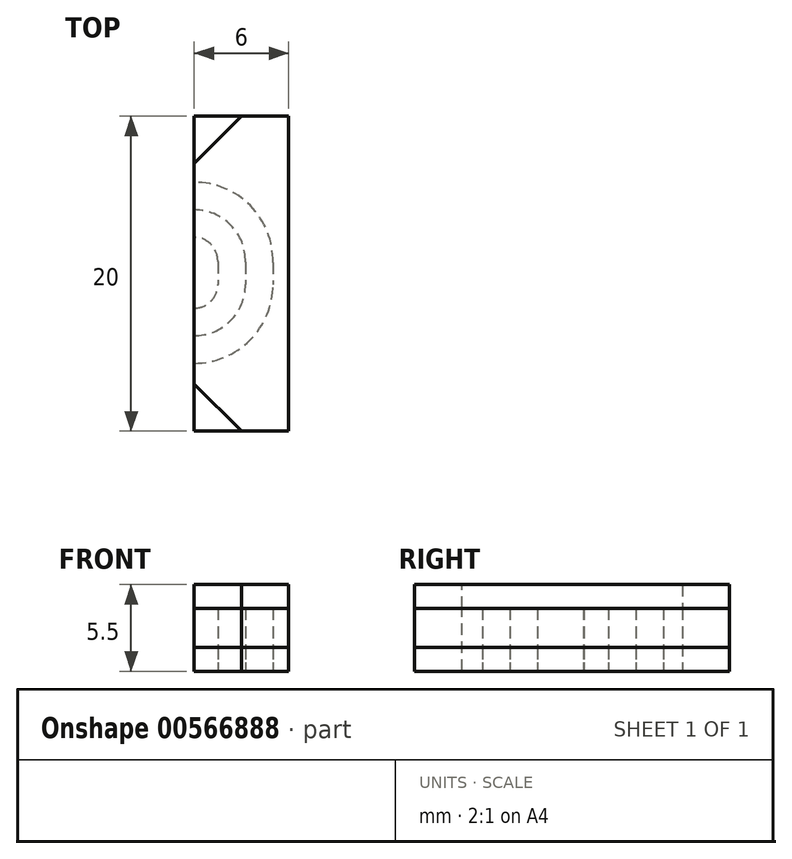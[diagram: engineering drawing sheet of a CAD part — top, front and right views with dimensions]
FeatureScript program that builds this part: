
annotation { "Feature Type Name" : "Feature", "Feature Type Description" : "" }
export const myFeature = defineFeature(function(context is Context, id is Id, definition is map)
    precondition{}
    {
        {
            var Q0;
            Q0=qCreatedBy(makeId("Top.planeOp"),FACE);
            var sketch = newSketch(context, id + "F0", { "sketchPlane" : qUnion([Q0])});
            skLineSegment(sketch, "E0.bottom", {"start": v(3, 10) * mm, "end": v(-3, 10) * mm});
            skLineSegment(sketch, "E0.top", {"start": v(3, -10) * mm, "end": v(-3, -10) * mm});
            skLineSegment(sketch, "E0.left", {"start": v(3, 10) * mm, "end": v(3, -10) * mm});
            skLineSegment(sketch, "E0.right", {"start": v(-3, 10) * mm, "end": v(-3, 5.81) * mm});
            skPoint(sketch, "E0.middle", {"position": v(0, 0) * mm});
            skArc(sketch, "E1", {"start": v(-1.5, 0.76) * mm, "mid": v(-1.92, 1.86) * mm, "end": v(-3, 2.31) * mm});
            skArc(sketch, "E2", {"start": v(-3, -2.19) * mm, "mid": v(-1.94, -1.75) * mm, "end": v(-1.5, -0.69) * mm});
            skLineSegment(sketch, "E3", {"start": v(-1.5, 0.76) * mm, "end": v(-1.5, -0.69) * mm});
            skLineSegment(sketch, "E4.trimOffspring", {"start": v(-3, -2.19) * mm, "end": v(-3, -3.94) * mm});
            skArc(sketch, "E5.0", {"start": v(-3, -3.94) * mm, "mid": v(-0.7, -2.99) * mm, "end": v(0.25, -0.69) * mm});
            skLineSegment(sketch, "E5.1", {"start": v(0.25, 0.74) * mm, "end": v(0.25, -0.69) * mm});
            skArc(sketch, "E5.2", {"start": v(0.25, 0.74) * mm, "mid": v(-0.68, 3.08) * mm, "end": v(-3, 4.06) * mm});
            skArc(sketch, "E6.0", {"start": v(2, 0.73) * mm, "mid": v(0.57, 4.32) * mm, "end": v(-3, 5.81) * mm});
            skLineSegment(sketch, "E6.1", {"start": v(2, 0.73) * mm, "end": v(2, -0.69) * mm});
            skArc(sketch, "E6.2", {"start": v(-3, -5.69) * mm, "mid": v(0.54, -4.22) * mm, "end": v(2, -0.69) * mm});
            skLineSegment(sketch, "E7.trimOffspring", {"start": v(-3, 4.06) * mm, "end": v(-3, 2.31) * mm});
            skLineSegment(sketch, "E8.trimOffspring", {"start": v(-3, -5.69) * mm, "end": v(-3, -10) * mm});
            skSolve(sketch);
        }
        {
            var Q0;
            Q0 = qSketchRegion(id + "F0", true);
            extrude(context, id + "F1", {"entities" : qUnion([Q0]), "depth" : 4 * mm, "offsetDistance" : 25 * mm});
        }
        {
            var Q0;
            Q0=qCreatedBy(makeId("Top.planeOp"),FACE);
            var sketch = newSketch(context, id + "F2", { "sketchPlane" : qUnion([Q0])});
            skLineSegment(sketch, "E9.bottom", {"start": v(3, -10) * mm, "end": v(-3, -10) * mm});
            skLineSegment(sketch, "E9.top", {"start": v(3, 10) * mm, "end": v(-3, 10) * mm});
            skLineSegment(sketch, "E9.left", {"start": v(3, -10) * mm, "end": v(3, 10) * mm});
            skLineSegment(sketch, "E9.right", {"start": v(-3, -10) * mm, "end": v(-3, 10) * mm});
            skPoint(sketch, "E9.middle", {"position": v(0, 0) * mm});
            skPoint(sketch, "E10", {"position": v(-3, -0.67) * mm});
            skPoint(sketch, "E11", {"position": v(-3, 0.83) * mm});
            skCircle(sketch, "E12", {"center": v(-3, -0.67) * mm, "radius": 1.5 * mm});
            skCircle(sketch, "E13", {"center": v(-3, 0.83) * mm, "radius": 1.5 * mm});
            skLineSegment(sketch, "E14", {"start": v(-1.5, -0.6) * mm, "end": v(-1.5, 0.84) * mm});
            skLineSegment(sketch, "E15", {"start": v(-4.47, -0.92) * mm, "end": v(-4.5, 0.8) * mm});
            skSolve(sketch);
        }
        {
            var Q0;
            Q0=makeQuery(id+"F1.opExtrude","CAP_FACE",FACE,{"disambiguationData":[OSD([sQuery(id+"F0.wireOp",EDGE,"E0.bottom"),sQuery(id+"F0.wireOp",EDGE,"E0.top"),sQuery(id+"F0.wireOp",EDGE,"E0.left"),sQuery(id+"F0.wireOp",EDGE,"E0.right"),sQuery(id+"F0.wireOp",EDGE,"E6.0"),sQuery(id+"F0.wireOp",EDGE,"E6.1"),sQuery(id+"F0.wireOp",EDGE,"E6.2"),sQuery(id+"F0.wireOp",EDGE,"E8.trimOffspring")])],"isStart":false});
            var sketch = newSketch(context, id + "F3", { "sketchPlane" : qUnion([Q0])});
            skLineSegment(sketch, "E16.bottom", {"start": v(-3, 10) * mm, "end": v(3, 10) * mm});
            skLineSegment(sketch, "E16.top", {"start": v(-3, -10) * mm, "end": v(3, -10) * mm});
            skLineSegment(sketch, "E16.left", {"start": v(-3, 10) * mm, "end": v(-3, -10) * mm});
            skLineSegment(sketch, "E16.right", {"start": v(3, 10) * mm, "end": v(3, -10) * mm});
            skSolve(sketch);
        }
        {
            var Q0;
            Q0 = qSketchRegion(id + "F3", true);
            var Q1;
            Q1 = qSketchRegion(id + "F0", true);
            extrude(context, id + "F4", {"entities" : qUnion([Q0, Q1]), "depth" : 1.5 * mm, "offsetDistance" : 25 * mm});
        }
        {
            var Q0;
            Q0=makeQuery(id+"F4.opExtrude","SWEPT_EDGE",EDGE,{"disambiguationData":[OSD([sQuery(id+"F3.wireOp",EDGE,"E16.bottom"),sQuery(id+"F3.wireOp",EDGE,"E16.left")])]});
            var Q1;
            Q1=makeQuery(id+"F1.opExtrude","SWEPT_EDGE",EDGE,{"disambiguationData":[OSD([sQuery(id+"F0.wireOp",EDGE,"E0.bottom"),sQuery(id+"F0.wireOp",EDGE,"E0.right")])]});
            var Q2;
            Q2=makeQuery(id+"F9HQLEJWvNsX2Ko_2.opExtrude","SWEPT_EDGE",EDGE,{"disambiguationData":[OSD([sQuery(id+"F2.wireOp",EDGE,"E9.top"),sQuery(id+"F2.wireOp",EDGE,"E9.right")])]});
            var Q3;
            Q3=makeQuery(id+"F9HQLEJWvNsX2Ko_2.opExtrude","SWEPT_EDGE",EDGE,{"disambiguationData":[OSD([sQuery(id+"F2.wireOp",EDGE,"E9.bottom"),sQuery(id+"F2.wireOp",EDGE,"E9.right")])]});
            var Q4;
            Q4=makeQuery(id+"F1.opExtrude","SWEPT_EDGE",EDGE,{"disambiguationData":[OSD([sQuery(id+"F0.wireOp",EDGE,"E0.top"),sQuery(id+"F0.wireOp",EDGE,"E8.trimOffspring")])]});
            var Q5;
            Q5=makeQuery(id+"F4.opExtrude","SWEPT_EDGE",EDGE,{"disambiguationData":[OSD([sQuery(id+"F3.wireOp",EDGE,"E16.top"),sQuery(id+"F3.wireOp",EDGE,"E16.left")])]});
            chamfer(context, id + "F5", {"entities" : qUnion([Q0, Q1, Q2, Q3, Q4, Q5]), "width" : 3 * mm, "tangentPropagation" : true});
        }
    });
